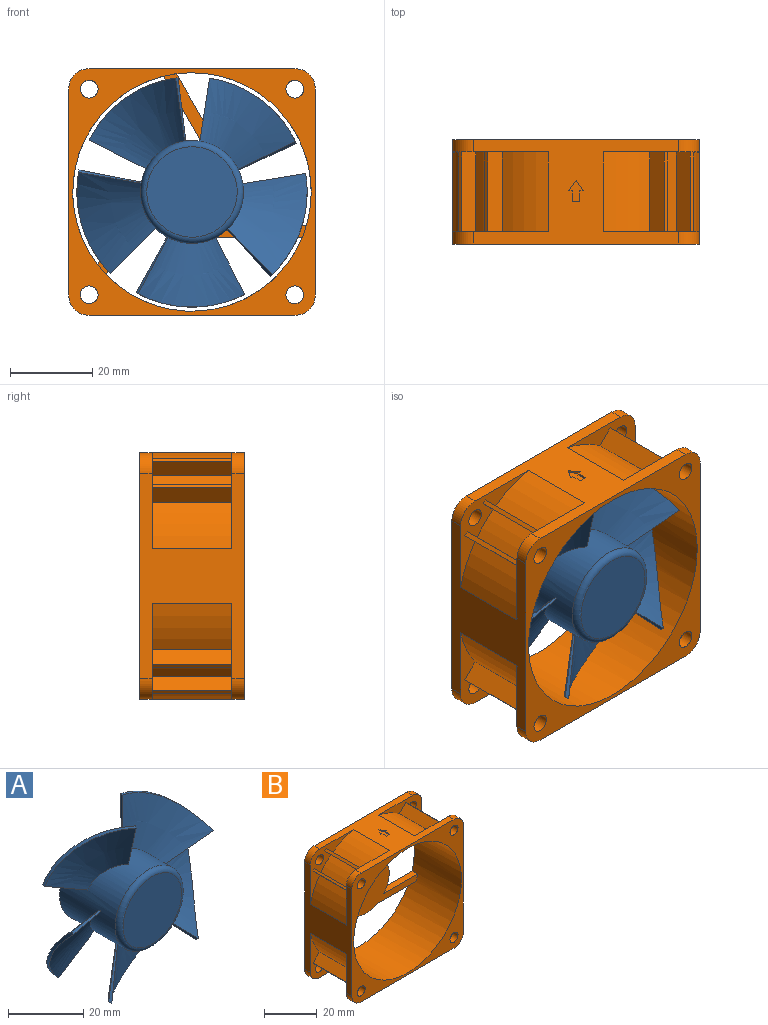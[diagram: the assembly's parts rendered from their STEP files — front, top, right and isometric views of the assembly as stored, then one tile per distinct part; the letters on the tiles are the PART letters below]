
ASSEMBLY  parts=2 mates=1
PART A: 29 faces, bbox 62.5x22.4x59.6 mm
  f0: cylinder r=12.5mm len=25mm, axis (0,-1,0), area 1611.7mm2, adj f1,f2,f3,f4,f5,f6,f7,f8
  f1: torus R=11mm, axis (0,1,0), area 177mm2, adj f0,f23
  f2: plane 25x25mm, normal (0,1,0), area 490.9mm2, adj f0
  f3: bspline ~26.4x15.23mm, area 285.4mm2, adj f0,f4,f6,f24
  f4: plane 13.82x7.14mm, normal (0.88,0.11,0.47), area 9.8mm2, adj f0,f3,f5,f24
  f5: bspline ~30.14x20.07mm, area 355.6mm2, adj f0,f4,f6,f24
  f6: plane 13.83x7.76mm, normal (-0.57,-0.63,0.53), area 10.5mm2, adj f0,f3,f5,f24
  f7: bspline ~28.18x23.24mm, area 295.3mm2, adj f0,f8,f10,f25
  f8: plane 11.04x10.97mm, normal (0.72,0.11,-0.69), area 9.8mm2, adj f0,f7,f9,f25
  f9: bspline ~28.77x23.41mm, area 299.4mm2, adj f0,f8,f10,f25
  f10: plane 15.32x5.33mm, normal (0.33,-0.63,0.7), area 10.5mm2, adj f0,f7,f9,f25
  f11: bspline ~27.36x26.02mm, area 295.3mm2, adj f0,f12,f14,f26
  f12: plane 13.86x7.05mm, normal (-0.43,0.11,-0.9), area 9.8mm2, adj f0,f11,f13,f26
  f13: bspline ~24.16x22.14mm, area 299.4mm2, adj f0,f12,f14,f26
  f14: plane 15.42x5.33mm, normal (0.77,-0.63,-0.1), area 10.5mm2, adj f0,f11,f13,f26
  f15: bspline ~23.46x23.23mm, area 295.3mm2, adj f0,f16,f18,f27
  f16: plane 15.33x3.22mm, normal (-0.99,0.11,0.14), area 9.8mm2, adj f0,f15,f17,f27
  f17: bspline ~23.45x23.26mm, area 299.4mm2, adj f0,f16,f18,f27
  f18: plane 14.17x7.08mm, normal (0.15,-0.63,-0.76), area 10.5mm2, adj f0,f15,f17,f27
  f19: bspline ~27.43x24.84mm, area 295.3mm2, adj f0,f20,f22,f28
  f20: plane 15.31x3.22mm, normal (-0.18,0.11,0.98), area 9.8mm2, adj f0,f19,f21,f28
  f21: bspline ~28x24.86mm, area 299.4mm2, adj f0,f20,f22,f28
  f22: plane 11.53x10.99mm, normal (-0.68,-0.63,-0.38), area 10.5mm2, adj f0,f19,f21,f28
  f23: plane 22x22mm, normal (0,-1,0), area 380.1mm2, adj f1
  f24: bspline ~28.52x17.06mm, area 29.9mm2, adj f3,f4,f5,f6
  f25: bspline ~27.4x17.06mm, area 29.9mm2, adj f7,f8,f9,f10
  f26: bspline ~23.61x17.06mm, area 29.9mm2, adj f11,f12,f13,f14
  f27: bspline ~22.53x17.5mm, area 29.9mm2, adj f15,f16,f17,f18
  f28: bspline ~26.84x17.06mm, area 29.9mm2, adj f19,f20,f21,f22
PART B: 85 faces, bbox 60x25.4x60 mm
  f0: cylinder r=2.16mm len=4.32mm, axis (0,1,0), area 40.7mm2, adj f64,f68
  f1: cylinder r=2.16mm len=4.32mm, axis (0,1,0), area 40.7mm2, adj f41,f70
  f2: cylinder r=2.16mm len=4.32mm, axis (0,1,0), area 40.7mm2, adj f41,f53
  f3: cylinder r=2.16mm len=4.32mm, axis (0,1,0), area 40.7mm2, adj f41,f59
  f4: cylinder r=2.16mm len=4.32mm, axis (0,1,0), area 40.7mm2, adj f41,f79
  f5: cylinder r=29mm len=58mm, axis (0,1,0), area 4599.6mm2, adj f32,f33,f35,f36,f38,f39,f40,f41
  f6: cylinder r=2.16mm len=4.32mm, axis (0,1,0), area 40.7mm2, adj f51,f64
  f7: cylinder r=2.16mm len=4.32mm, axis (0,1,0), area 40.7mm2, adj f63,f64
  f8: cylinder r=2.16mm len=4.32mm, axis (0,1,0), area 40.7mm2, adj f64,f77
  f9: plane 19.4x0.76mm, normal (-0.71,0,-0.71), area 20.7mm2, adj f10,f77,f79,f81
  f10: plane 19.4x3.55mm, normal (-0.71,0,0.71), area 97.3mm2, adj f9,f11,f77,f79
  f11: cylinder r=30.75mm len=19.4mm, axis (0,-1,0), area 239.1mm2, adj f10,f71,f77,f79
  f12: cylinder r=5mm len=5mm, axis (0,1,0), area 23.6mm2, adj f64,f71,f73,f77
  f13: plane 1.76x0.5mm, normal (0,1,0), area 0.9mm2, adj f14,f19,f20,f56
  f14: plane 2.5x0.5mm, normal (1,0,0), area 1.3mm2, adj f13,f15,f19,f56
  f15: plane 0.87x0.5mm, normal (0,1,0), area 0.4mm2, adj f14,f16,f19,f56
  f16: plane 2.5x1.75mm, normal (0.82,-0.57,0), area 1.5mm2, adj f15,f17,f19,f56
  f17: plane 2.5x1.75mm, normal (-0.82,-0.57,0), area 1.5mm2, adj f16,f18,f19,f56
  f18: plane 0.87x0.5mm, normal (0,1,0), area 0.4mm2, adj f17,f19,f20,f56
  f19: plane 5x3.5mm, normal (0,0,1), area 8.8mm2, adj f13,f14,f15,f16,f17,f18,f20
  f20: plane 2.5x0.5mm, normal (-1,0,0), area 1.3mm2, adj f13,f18,f19,f56
  f21: cylinder r=30.75mm len=19.4mm, axis (0,-1,0), area 152.9mm2, adj f22,f68,f70,f82
  f22: plane 19.4x3.44mm, normal (-0.71,0,-0.71), area 94.2mm2, adj f21,f23,f68,f70
  f23: plane 19.4x0.76mm, normal (-0.71,0,0.71), area 20.7mm2, adj f22,f24,f68,f70
  f24: plane 19.4x3.55mm, normal (0.71,0,0.71), area 97.3mm2, adj f23,f25,f68,f70
  f25: cylinder r=30.75mm len=19.4mm, axis (0,-1,0), area 239.1mm2, adj f24,f56,f68,f70
  f26: cylinder r=5mm len=5mm, axis (0,1,0), area 23.6mm2, adj f54,f56,f63,f64
  f27: plane 19.4x0.76mm, normal (0.71,0,0.71), area 20.7mm2, adj f28,f59,f63,f83
  f28: plane 19.4x3.55mm, normal (0.71,0,-0.71), area 97.3mm2, adj f27,f29,f59,f63
  f29: cylinder r=30.75mm len=19.4mm, axis (0,-1,0), area 239.1mm2, adj f28,f54,f59,f63
  f30: cylinder r=5mm len=5mm, axis (0,1,0), area 23.6mm2, adj f41,f56,f70,f71
  f31: cylinder r=12.5mm len=14.71mm, axis (0,1,0), area 64.1mm2, adj f32,f39,f40,f41
  f32: plane 15.86x9.16mm, normal (-0.87,0,-0.5), area 54.9mm2, adj f5,f31,f39,f41
  f33: plane 18.19x10.5mm, normal (0.87,0,0.5), area 63mm2, adj f5,f34,f39,f41
  f34: cylinder r=12.5mm len=18.63mm, axis (0,1,0), area 64.1mm2, adj f33,f35,f39,f41
  f35: plane 18.31x3mm, normal (0,0,1), area 54.9mm2, adj f5,f34,f39,f41
  f36: plane 21.01x3mm, normal (0,0,-1), area 63mm2, adj f5,f37,f39,f41
  f37: cylinder r=12.5mm len=17.56mm, axis (0,1,0), area 64.1mm2, adj f36,f38,f39,f41
  f38: plane 15.86x9.16mm, normal (0.87,0,-0.5), area 54.9mm2, adj f5,f37,f39,f41
  f39: plane 50.85x48.83mm, normal (0,-1,0), area 665.8mm2, adj f5,f31,f32,f33,f34,f35,f36,f37
  f40: plane 18.19x10.5mm, normal (-0.87,0,0.5), area 63mm2, adj f5,f31,f39,f41
  f41: plane 60x60mm, normal (0,1,0), area 1543.7mm2, adj f1,f2,f3,f4,f5,f30,f31,f32
  f42: cylinder r=5mm len=5mm, axis (0,1,0), area 23.6mm2, adj f41,f53,f54,f73
  f43: cylinder r=30.75mm len=19.4mm, axis (0,-1,0), area 152.9mm2, adj f44,f51,f53,f84
  f44: plane 19.4x3.44mm, normal (0.71,0,0.71), area 94.2mm2, adj f43,f45,f51,f53
  f45: plane 19.4x0.76mm, normal (0.71,0,-0.71), area 20.7mm2, adj f44,f46,f51,f53
  f46: plane 19.4x3.55mm, normal (-0.71,0,-0.71), area 97.3mm2, adj f45,f47,f51,f53
  f47: cylinder r=30.75mm len=19.4mm, axis (0,-1,0), area 239.1mm2, adj f46,f51,f53,f73
  f48: cylinder r=5mm len=5mm, axis (0,1,0), area 23.6mm2, adj f51,f54,f64,f73
  f49: plane 19.4x3.55mm, normal (0.71,0,0.71), area 97.3mm2, adj f50,f51,f52,f53
  f50: plane 19.4x0.76mm, normal (0.71,0,-0.71), area 20.7mm2, adj f49,f51,f53,f84
  f51: plane 23.25x23.25mm, normal (0,1,0), area 133.6mm2, adj f6,f43,f44,f45,f46,f47,f48,f49
  f52: cylinder r=30.75mm len=19.4mm, axis (0,-1,0), area 239.1mm2, adj f49,f51,f53,f54
  f53: plane 23.25x23.25mm, normal (0,-1,0), area 133.6mm2, adj f2,f42,f43,f44,f45,f46,f47,f49
  f54: plane 50x25.4mm, normal (1,0,0), area 561.9mm2, adj f26,f29,f41,f42,f48,f51,f52,f53
  f55: cylinder r=5mm len=5mm, axis (0,1,0), area 23.6mm2, adj f41,f54,f56,f59
  f56: plane 50x25.4mm, normal (0,0,1), area 553.1mm2, adj f13,f14,f15,f16,f17,f18,f20,f25
  f57: plane 19.4x3.55mm, normal (-0.71,0,0.71), area 97.3mm2, adj f58,f59,f62,f63
  f58: cylinder r=30.75mm len=19.4mm, axis (0,-1,0), area 239.1mm2, adj f56,f57,f59,f63
  f59: plane 23.25x23.25mm, normal (0,-1,0), area 133.6mm2, adj f3,f27,f28,f29,f54,f55,f56,f57
  f60: cylinder r=30.75mm len=19.4mm, axis (0,-1,0), area 152.9mm2, adj f59,f61,f63,f83
  f61: plane 19.4x3.44mm, normal (0.71,0,-0.71), area 94.2mm2, adj f59,f60,f62,f63
  f62: plane 19.4x0.76mm, normal (0.71,0,0.71), area 20.7mm2, adj f57,f59,f61,f63
  f63: plane 23.25x23.25mm, normal (0,1,0), area 133.6mm2, adj f7,f26,f27,f28,f29,f54,f56,f57
  f64: plane 60x60mm, normal (0,-1,0), area 877.9mm2, adj f0,f5,f6,f7,f8,f12,f26,f48
  f65: cylinder r=5mm len=5mm, axis (0,1,0), area 23.6mm2, adj f56,f64,f68,f71
  f66: plane 19.4x3.55mm, normal (-0.71,0,-0.71), area 97.3mm2, adj f67,f68,f69,f70
  f67: plane 19.4x0.76mm, normal (-0.71,0,0.71), area 20.7mm2, adj f66,f68,f70,f82
  f68: plane 23.25x23.25mm, normal (0,1,0), area 133.6mm2, adj f0,f21,f22,f23,f24,f25,f56,f65
  f69: cylinder r=30.75mm len=19.4mm, axis (0,-1,0), area 239.1mm2, adj f66,f68,f70,f71
  f70: plane 23.25x23.25mm, normal (0,-1,0), area 133.6mm2, adj f1,f21,f22,f23,f24,f25,f30,f56
  f71: plane 50x25.4mm, normal (-1,0,0), area 561.9mm2, adj f11,f12,f30,f41,f64,f65,f68,f69
  f72: cylinder r=5mm len=5mm, axis (0,1,0), area 23.6mm2, adj f41,f71,f73,f79
  f73: plane 50x25.4mm, normal (0,0,-1), area 561.9mm2, adj f12,f41,f42,f47,f48,f51,f53,f64
  f74: cylinder r=30.75mm len=19.4mm, axis (0,-1,0), area 152.9mm2, adj f75,f77,f79,f81
  f75: plane 19.4x3.44mm, normal (-0.71,0,0.71), area 94.2mm2, adj f74,f76,f77,f79
  f76: plane 19.4x0.76mm, normal (-0.71,0,-0.71), area 20.7mm2, adj f75,f77,f79,f80
  f77: plane 23.25x23.25mm, normal (0,1,0), area 133.6mm2, adj f8,f9,f10,f11,f12,f71,f73,f74
  f78: cylinder r=30.75mm len=19.4mm, axis (0,-1,0), area 239.1mm2, adj f73,f77,f79,f80
  f79: plane 23.25x23.25mm, normal (0,-1,0), area 133.6mm2, adj f4,f9,f10,f11,f71,f72,f73,f74
  f80: plane 19.4x3.55mm, normal (0.71,0,-0.71), area 97.3mm2, adj f76,f77,f78,f79
  f81: plane 19.4x3.44mm, normal (0.71,0,-0.71), area 94.2mm2, adj f9,f74,f77,f79
  f82: plane 19.4x3.44mm, normal (0.71,0,0.71), area 94.2mm2, adj f21,f67,f68,f70
  f83: plane 19.4x3.44mm, normal (-0.71,0,0.71), area 94.2mm2, adj f27,f59,f60,f63
  f84: plane 19.4x3.44mm, normal (-0.71,0,-0.71), area 94.2mm2, adj f43,f50,f51,f53
PLACE A t=(-2.75,24.35,0.8)mm
PLACE B t=(-2.75,24.35,0.8)mm
MATE revolute B.f5 <-> A.f1  axis (0,-1,0) through (-2.75,21.35,0.8)mm
